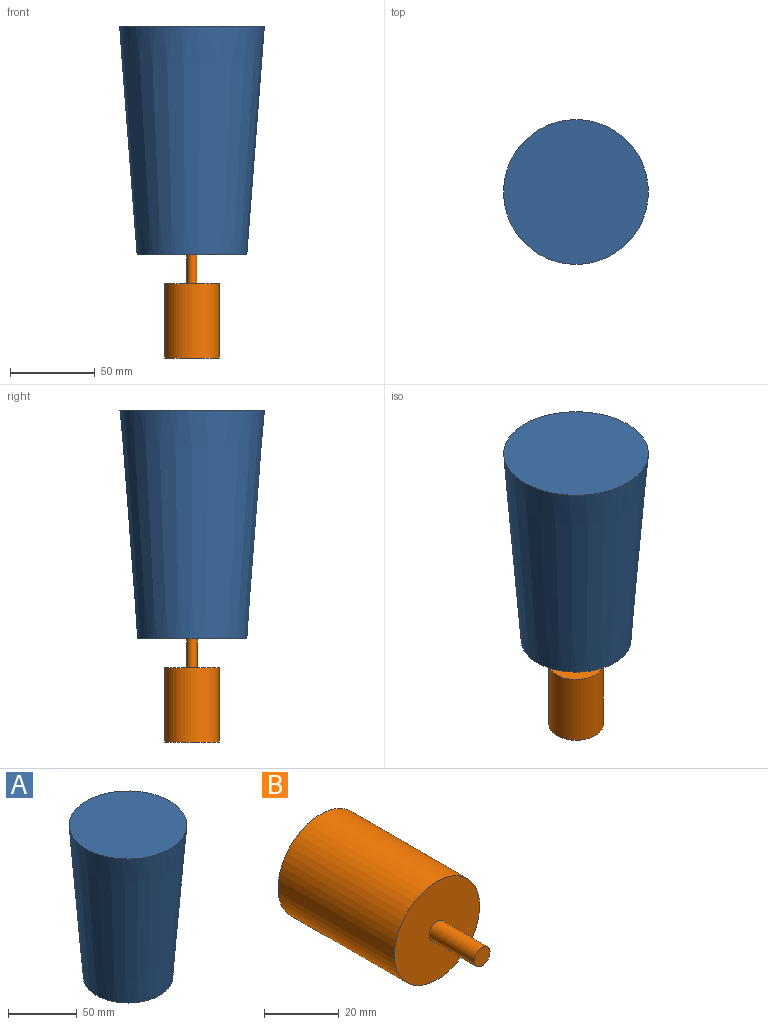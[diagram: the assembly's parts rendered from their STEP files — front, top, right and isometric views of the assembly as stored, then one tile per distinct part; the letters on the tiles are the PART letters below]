
ASSEMBLY  parts=2 mates=1
PART A: 3 faces, bbox 85.6x85.6x135.4 mm
  f0: plane 64.92x64.92mm, normal (0,0,-1), area 3310.4mm2, adj f2
  f1: plane 85.65x85.65mm, normal (0,0,1), area 5761.5mm2, adj f2
  f2: cone r=32.46mm half-angle=4.4deg, axis (0,0,1), area 32113.8mm2, adj f0,f1
PART B: 5 faces, bbox 32.1x61x32.1 mm
  f0: cylinder r=16.07mm len=43.94mm, axis (0,1,0), area 4435.6mm2, adj f1,f2
  f1: plane 32.13x32.13mm, normal (0,-1,0), area 782.6mm2, adj f0,f3
  f2: plane 32.13x32.13mm, normal (0,1,0), area 810.8mm2, adj f0
  f3: cylinder r=3mm len=17.02mm, axis (0,1,0), area 320.5mm2, adj f1,f4
  f4: plane 5.99x5.99mm, normal (0,-1,0), area 28.2mm2, adj f3
PLACE A at identity
PLACE B rot(axis=(-1,0,0),90deg) t=(0,0,-60.96)mm
MATE revolute B.f3 <-> A.f2  axis (0,0,1) through (0,0,0)mm
